# Revit family: Plumbing-Faucet-Sloan-Valve-EAF-275
name_source: partatom
category: Plumbing Fixtures
units: mm (PartAtom-declared; Revit-internal decimal feet)

## family parameters
Cut with Voids When Loaded = No
Host = Face
OmniClass Number = 23.45.55.14
OmniClass Title = Single Faucets
Part Type = Normal
Room Calculation Point = No
Round Connector Dimension = Use Diameter
Shared = No

## types (12) — shared parameters
Assembly Code = D2010
CW Connection = Yes
CWFU = 1.5
Cold Water Connection Diameter = 0"
Default Elevation = 0"
Depth = 5 3/8"
Edition number = 1
HW Connection = Yes
HWFU = 1.5
Height = 5 3/8"
Hot Water Connection Diameter = 0"
Keynote = 15410
Manufacturer = Sloan Valve
Product data url = https://bimobject.com
URL = www.sloanvalve.com
Valve Pressure Drop = 0.00 psi
Vent Connection = No
Waste Connection = No
zero-valued in all types: WFU

## per-type parameters (varying)
| type | Description | Part Number | Product Material | Water Flow |
| EAF-275-SOL-CP-0.35GPM-MLM-IR-IQ-CO-FCT | Solar Power Supply, Mixer Not Included, Polished Chrome Finish, 0.35 gpm, Multi-Laminar Spray, Infrared Sensor, Optima® Solar-Powered Deck-Mounted Mid Body Faucet. | 3335152T | Sloan Valve - Finish - Polished Chrome | 0 GPM |
| EAF-275-SOL-CP-0.35GPM-MLM-IR-IQ-FCT | Solar Power Supply, Mixer Not Included, Polished Chrome Finish, 0.35 gpm, Multi-Laminar Spray, Infrared Sensor, Optima® Solar-Powered Deck-Mounted Mid Body Faucet. | 3335152 | Sloan Valve - Finish - Polished Chrome | 0 GPM |
| EAF-275-SOL-CP-0.5GPM-AER-IR-IQ-FCT | Solar Power Supply, Mixer Not Included, Polished Chrome Finish, 0.5 gpm, Aerated Spray, Infrared Sensor, Optima® Solar-Powered DeckMounted Mid Body Faucet. | 3335016 | Sloan Valve - Finish - Polished Chrome | 1 GPM |
| EAF-275-SOL-ISM-BN-0.5GPM-AER-IR-IQ-FCT | Solar Power Supply, Integrated Side Mixer, Brushed Nickel Finish, 0.5 gpm, Aerated Spray, Infrared Sensor, Optima® Solar-Powered DeckMounted Mid Body Faucet. | 3335070 | Sloan Valve - Finish - Brushed Nickel | 1 GPM |
| EAF-275-SOL-ISM-CP-0.35GPM-MLM-IR-IQ-FCT | Solar Power Supply, Integrated Side Mixer, Polished Chrome Finish, 0.35 gpm, Multi-Laminar Spray, Infrared Sensor, Optima® SolarPowered Deck-Mounted Mid Body Faucet. | 3335150 | Sloan Valve - Finish - Polished Chrome | 0 GPM |
| EAF-275-SOL-ISM-CP-0.5GPM-AER-IR-IQ-EXT-FCT | Solar Power Supply, Integrated Side Mixer, Polished Chrome Finish, 0.5 gpm, Aerated Spray, Infrared Sensor, Optima® Solar-Powered Deck-Mounted Mid Body Faucet. | 3335047 | Sloan Valve - Finish - Polished Chrome | 1 GPM |
| EAF-275-SOL-ISM-CP-0.5GPM-AER-IR-IQ-FCT | Solar Power Supply, Integrated Side Mixer, Polished Chrome Finish, 0.5 gpm, Aerated Spray, Infrared Sensor, Optima® Solar-Powered Deck-Mounted Mid Body Faucet. | 3335017 | Sloan Valve - Finish - Polished Chrome | 1 GPM |
| EAF-275-SOL-ISM-PB-0.5GPM-AER-IR-IQ-FCT | Solar Power Supply, Integrated Side Mixer, Polished Brass Finish, 0.5 gpm, Aerated Spray, Infrared Sensor, Optima® Solar-Powered DeckMounted Mid Body Faucet. | 3335117 | Sloan Valve - Finish - Polished Brass | 1 GPM |
| EAF-275-SOL-ISM-SF-0.5GPM-AER-IR-IQ-FCT | Solar Power Supply, Integrated Side Mixer, Brushed Stainless Finish, 0.5 gpm, Aerated Spray, Infrared Sensor, Optima® Solar-Powered Deck-Mounted Mid Body Faucet. | 3335092 | Sloan Valve - Stainless Steel - Brushed | 1 GPM |
| EAF-275-SOL-ITM-CP-0.35GPM-MLM-IR-IQ-FCT | Solar Power Supply, Integrated Thermostatic Mixer, Polished Chrome Finish, 0.35 gpm, Multi-Laminar Spray, Infrared Sensor, Optima® Solar-Powered Deck-Mounted Mid Body Faucet. | 3335189 | Sloan Valve - Finish - Polished Chrome | 0 GPM |
| EAF-275-SOL-ITM-CP-0.5GPM-AER-IR-IQ-FCT | Solar Power Supply, Integrated Thermostatic Mixer, Polished Chrome Finish, 0.5 gpm, Aerated Spray, Infrared Sensor, Optima® SolarPowered Deck-Mounted Mid Body Faucet. | 3335190 | Sloan Valve - Finish - Polished Chrome | 1 GPM |
| EAF-275-SOL-ITM-CP-1.0GPM-LAM-IR-IQ-FCT | Solar Power Supply, Integrated Thermostatic Mixer, Polished ChromeFinish, 1.0 gpm, Laminar Spray, Infrared Sensor, Optima® SolarPowered Deck-Mounted Mid Body Faucet. | 3335191 | Sloan Valve - Finish - Polished Chrome | 1 GPM |

note: column(s) folded — value = type name in every type: Model

## geometry (parser evidence)
native form markers: Sweep x7
no freeform markers — native parametric forms only
